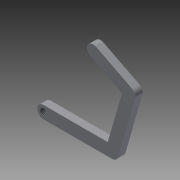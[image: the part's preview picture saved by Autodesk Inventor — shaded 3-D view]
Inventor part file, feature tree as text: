
AUTODESK INVENTOR PART (.ipt)
format: ipt  version: 2015 SP2 (Build 190223200, 223)  size: 93,696 bytes
history: native  units: mm
features: extrude x2, sketch x2, thread x1
ambient origin geometry x8: Origin, YZ Plane, XZ Plane, XY Plane, X Axis, Y Axis, Z Axis, Center Point
bodies: Solid1 (feature_tree)
feature tree (5):
  extrude  "Extrusion1"  Depth=5.0mm
  extrude  "Extrusion2"  Depth=10.0mm
  thread  "Thread2"  [1 undecoded]
  sketch  "Sketch1"  dims[d0=5.0mm d1=5.0mm]
  sketch  "Sketch2"  dims[d2=5.0mm d3=5.0mm d4=3.0mm d5=0.0mm d6=2.8mm d7=8.0mm d8=0.0mm d11=10.0mm d12=0.0mm]
note: 1 required parameter value undecoded (feature->parameter linkage not recoverable at this tier; creation-order binding heuristic only, values carry confidence <= 0.55)
